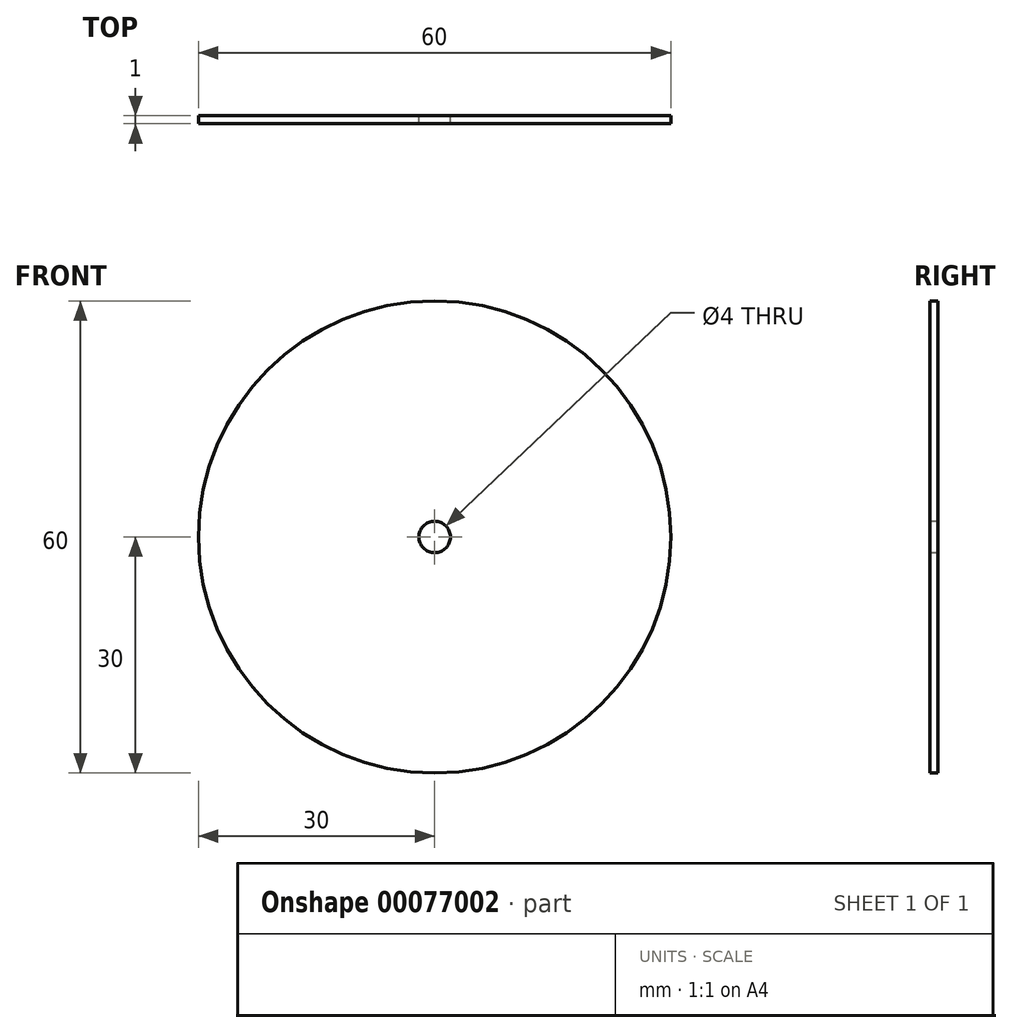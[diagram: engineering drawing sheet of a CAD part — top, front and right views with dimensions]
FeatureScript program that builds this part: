
annotation { "Feature Type Name" : "Feature", "Feature Type Description" : "" }
export const myFeature = defineFeature(function(context is Context, id is Id, definition is map)
    precondition{}
    {
        {
            var Q0;
            Q0=qCreatedBy(makeId("Front.planeOp"),FACE);
            var sketch = newSketch(context, id + "F0", { "sketchPlane" : qUnion([Q0])});
            skCircle(sketch, "E0", {"center": v(0, 0) * mm, "radius": 2 * mm});
            skCircle(sketch, "E1", {"center": v(0, 0) * mm, "radius": 30 * mm});
            skSolve(sketch);
        }
        {
            var Q0;
            Q0=makeQuery(id+"F0.imprint","IMPRINT",FACE,{"disambiguationData":[TD([[makeQuery(id+"F0.imprint","IMPRINT",EDGE,{"derivedFrom":sQuery(id+"F0.wireOp",EDGE,"E0")}),-1.0]])]});
            extrude(context, id + "F1", {"entities" : qUnion([Q0]), "depth" : 1 * mm});
        }
    });
